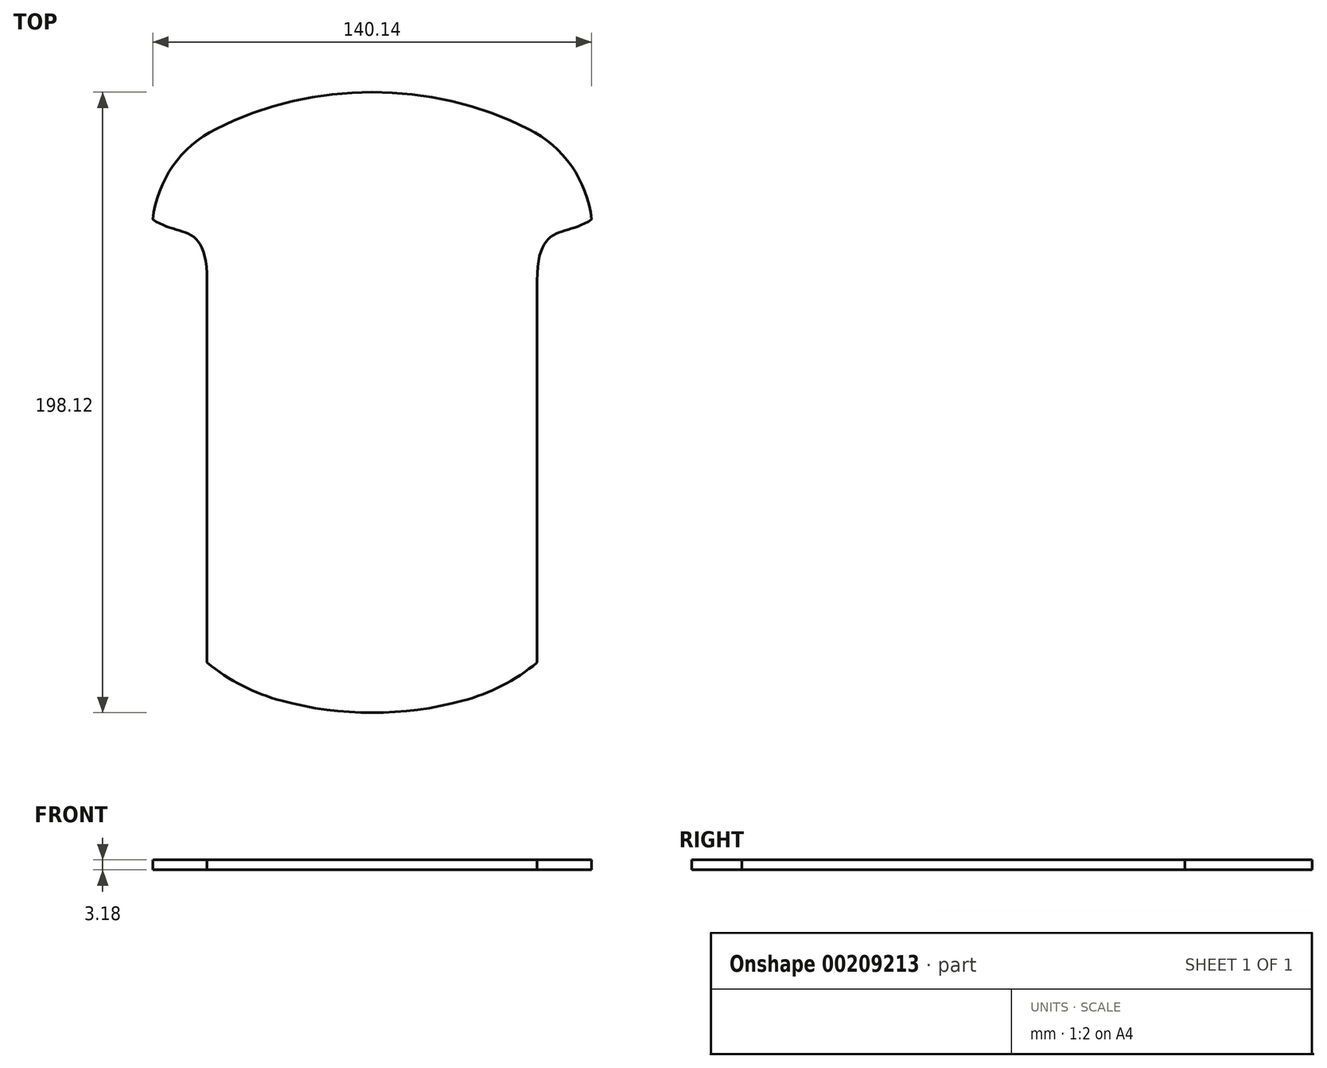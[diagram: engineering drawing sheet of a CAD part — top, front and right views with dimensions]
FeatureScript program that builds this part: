
annotation { "Feature Type Name" : "Feature", "Feature Type Description" : "" }
export const myFeature = defineFeature(function(context is Context, id is Id, definition is map)
    precondition{}
    {
        {
            var Q0;
            Q0=qCreatedBy(makeId("Top.planeOp"),FACE);
            var sketch = newSketch(context, id + "F0", { "sketchPlane" : qUnion([Q0])});
            skLineSegment(sketch, "E0", {"start": v(52.7, -90.68) * mm, "end": v(52.7, 31.24) * mm});
            skArc(sketch, "E1", {"start": v(70.07, 50.8) * mm, "mid": v(63.66, 67.8) * mm, "end": v(49.9, 79.68) * mm});
            skArc(sketch, "E2", {"start": v(49.9, 79.68) * mm, "mid": v(25.64, 88.46) * mm, "end": v(0, 91.44) * mm});
            skLineSegment(sketch, "E3", {"start": v(0, 91.44) * mm, "end": v(-25.6, 91.44) * mm, "construction": true});
            skLineSegment(sketch, "E4", {"start": v(0, -106.68) * mm, "end": v(-52.32, -106.68) * mm, "construction": true});
            skArc(sketch, "E5", {"start": v(0, -106.68) * mm, "mid": v(14.59, -105.72) * mm, "end": v(28.92, -102.87) * mm});
            skArc(sketch, "E6", {"start": v(28.92, -102.87) * mm, "mid": v(41.46, -98.04) * mm, "end": v(52.7, -90.68) * mm});
            skLineSegment(sketch, "E7", {"start": v(0, 91.44) * mm, "end": v(0, 0) * mm, "construction": true});
            skLineSegment(sketch, "E8", {"start": v(0, 0) * mm, "end": v(0, -106.68) * mm, "construction": true});
            skLineSegment(sketch, "E9", {"start": v(0, 0) * mm, "end": v(52.7, 0) * mm, "construction": true});
            skArc(sketch, "E10.MirrorCS", {"start": v(-49.9, 79.68) * mm, "mid": v(-25.64, 88.46) * mm, "end": v(0, 91.44) * mm});
            skArc(sketch, "E11.MirrorCS", {"start": v(-70.07, 50.8) * mm, "mid": v(-63.66, 67.8) * mm, "end": v(-49.9, 79.68) * mm});
            skLineSegment(sketch, "E12.MirrorCS", {"start": v(-52.7, -90.68) * mm, "end": v(-52.7, 31.24) * mm});
            skArc(sketch, "E13.MirrorCS", {"start": v(-28.92, -102.87) * mm, "mid": v(-41.46, -98.04) * mm, "end": v(-52.7, -90.68) * mm});
            skArc(sketch, "E14.MirrorCS", {"start": v(0, -106.68) * mm, "mid": v(-14.59, -105.72) * mm, "end": v(-28.92, -102.87) * mm});
            skFitSpline(sketch, "E15", {"points": [v(52.7, 31.24) * mm, v(70.07, 50.8) * mm], "startDerivative": vector(0, 57.15) * mm, "endDerivative": vector(25.15, 17.53) * mm});
            skLineSegment(sketch, "E16", {"start": v(52.7, 50.3) * mm, "end": v(52.7, 31.24) * mm, "construction": true});
            skFitSpline(sketch, "E17.MirrorCS", {"points": [v(-52.7, 31.24) * mm, v(-70.07, 50.8) * mm], "startDerivative": vector(0, 57.15) * mm, "endDerivative": vector(-25.15, 17.53) * mm});
            skSolve(sketch);
        }
        {
            var Q0;
            Q0 = qSketchRegion(id + "F0", true);
            extrude(context, id + "F1", {"entities" : qUnion([Q0]), "depth" : 3.17 * mm});
        }
    });
